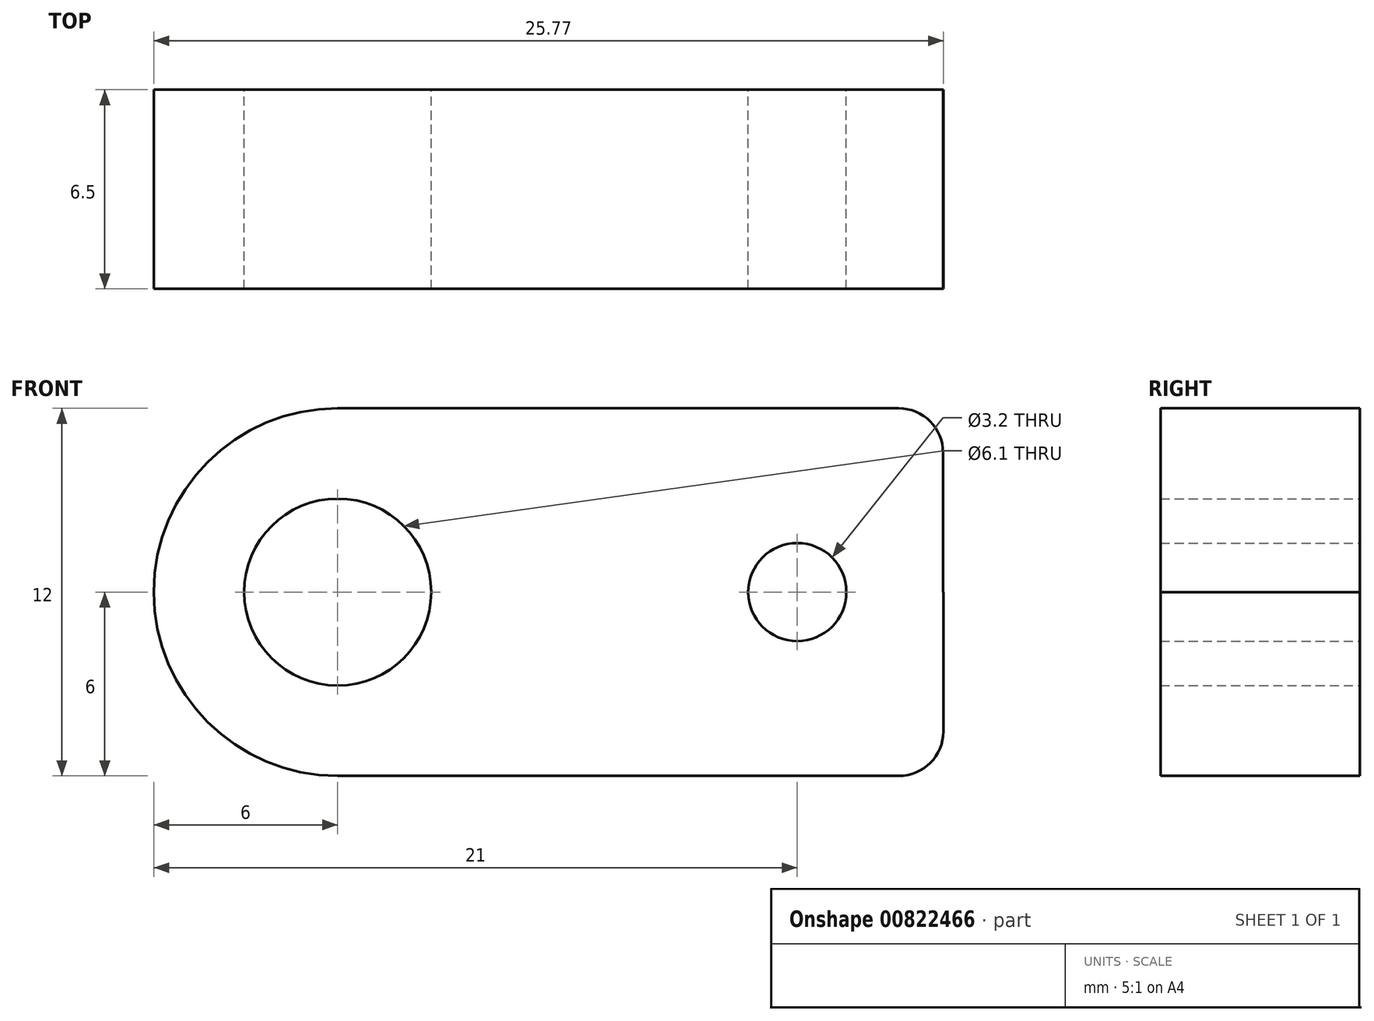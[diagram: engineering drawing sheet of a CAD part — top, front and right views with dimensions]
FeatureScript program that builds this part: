
annotation { "Feature Type Name" : "Feature", "Feature Type Description" : "" }
export const myFeature = defineFeature(function(context is Context, id is Id, definition is map)
    precondition{}
    {
        {
            var Q0;
            Q0=qCreatedBy(makeId("Front.planeOp"),FACE);
            var sketch = newSketch(context, id + "F0", { "sketchPlane" : qUnion([Q0])});
            skLineSegment(sketch, "E0.top", {"start": v(-15, 6) * mm, "end": v(4.76, 6) * mm});
            skLineSegment(sketch, "E0.right", {"start": v(4.76, 0) * mm, "end": v(4.76, 6) * mm});
            skLineSegment(sketch, "E1.bottom", {"start": v(4.76, 0) * mm, "end": v(4.77, 0) * mm});
            skLineSegment(sketch, "E1.top", {"start": v(-15, -6) * mm, "end": v(4.77, -6) * mm});
            skLineSegment(sketch, "E1.right", {"start": v(4.77, 0) * mm, "end": v(4.77, -6) * mm});
            skCircle(sketch, "E2", {"center": v(0, 0) * mm, "radius": 1.6 * mm});
            skCircle(sketch, "E3", {"center": v(-15, 0) * mm, "radius": 3.05 * mm});
            skArc(sketch, "E4", {"start": v(-15, 6) * mm, "mid": v(-21, 0) * mm, "end": v(-15, -6) * mm});
            skSolve(sketch);
        }
        {
            var Q0;
            Q0 = qSketchRegion(id + "F0", true);
            extrude(context, id + "F1", {"entities" : qUnion([Q0]), "depth" : 6.5 * mm, "offsetDistance" : 25 * mm});
        }
        {
            var Q0;
            Q0=makeQuery(id+"F1.opExtrude","SWEPT_EDGE",EDGE,{"disambiguationData":[OSD([sQuery(id+"F0.wireOp",EDGE,"E0.top"),sQuery(id+"F0.wireOp",EDGE,"E0.right")])]});
            var Q1;
            Q1=makeQuery(id+"F1.opExtrude","SWEPT_EDGE",EDGE,{"disambiguationData":[OSD([sQuery(id+"F0.wireOp",EDGE,"E1.top"),sQuery(id+"F0.wireOp",EDGE,"E1.right")])]});
            fillet(context, id + "F2", {"entities" : qUnion([Q0, Q1]), "radius" : 1.45 * mm, "tangentPropagation" : true, "allowEdgeOverflow" : false});
        }
    });
